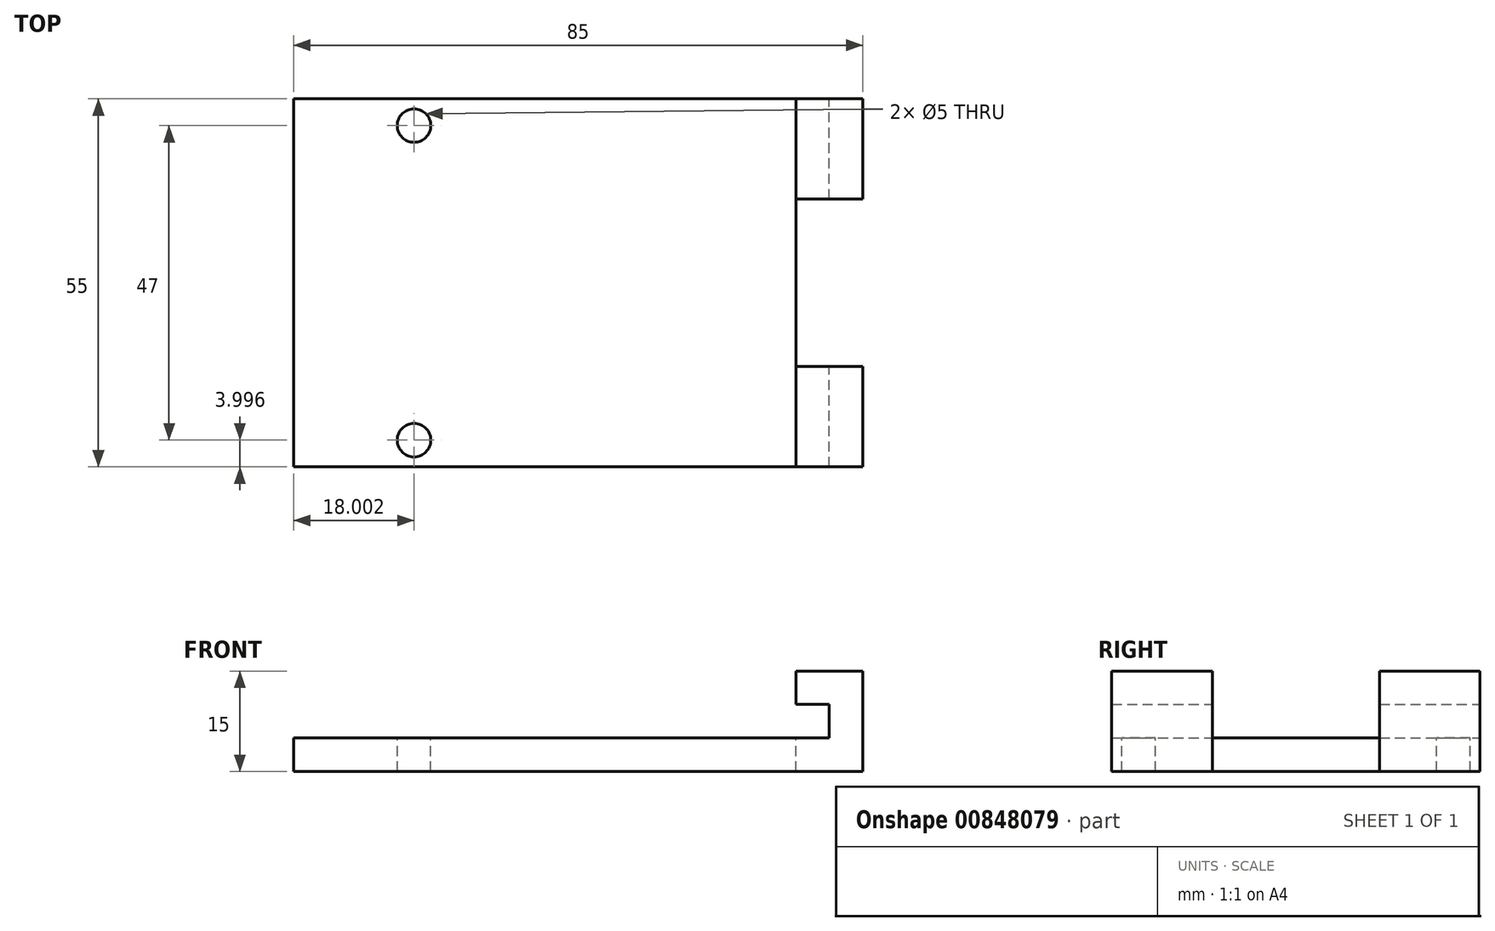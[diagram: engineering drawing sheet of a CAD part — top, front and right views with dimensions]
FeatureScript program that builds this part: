
annotation { "Feature Type Name" : "Feature", "Feature Type Description" : "" }
export const myFeature = defineFeature(function(context is Context, id is Id, definition is map)
    precondition{}
    {
        {
            var Q0;
            Q0=qCreatedBy(makeId("Top.planeOp"),FACE);
            var sketch = newSketch(context, id + "F0", { "sketchPlane" : qUnion([Q0])});
            skLineSegment(sketch, "E0.bottom", {"start": v(-43.19, 22.84) * mm, "end": v(41.81, 22.84) * mm});
            skLineSegment(sketch, "E0.top", {"start": v(-43.19, -32.16) * mm, "end": v(41.81, -32.16) * mm});
            skLineSegment(sketch, "E0.left", {"start": v(-43.19, 22.84) * mm, "end": v(-43.19, -32.16) * mm});
            skLineSegment(sketch, "E0.right", {"start": v(41.81, 22.84) * mm, "end": v(41.81, -32.16) * mm});
            skSolve(sketch);
        }
        {
            var Q0;
            Q0=makeQuery(id+"F0.imprint","IMPRINT",FACE,{"disambiguationData":[TD([[makeQuery(id+"F0.imprint","IMPRINT",EDGE,{"derivedFrom":sQuery(id+"F0.wireOp",EDGE,"E0.bottom")}),-1.0]])]});
            extrude(context, id + "F1", {"entities" : qUnion([Q0]), "depth" : 5 * mm, "offsetDistance" : 25 * mm});
        }
        {
            var Q0;
            Q0=makeQuery(id+"F1.opExtrude","SWEPT_FACE",FACE,{"disambiguationData":[OSD([sQuery(id+"F0.wireOp",EDGE,"E0.right")])]});
            var sketch = newSketch(context, id + "F2", { "sketchPlane" : qUnion([Q0])});
            skLineSegment(sketch, "E1.bottom", {"start": v(-32.16, 0) * mm, "end": v(22.84, 0) * mm});
            skLineSegment(sketch, "E1.top", {"start": v(-32.16, 10) * mm, "end": v(22.84, 10) * mm});
            skLineSegment(sketch, "E1.left", {"start": v(-32.16, 0) * mm, "end": v(-32.16, 10) * mm});
            skLineSegment(sketch, "E1.right", {"start": v(22.84, 0) * mm, "end": v(22.84, 10) * mm});
            skSolve(sketch);
        }
        {
            var Q0;
            Q0 = qSketchRegion(id + "F2", true);
            extrude(context, id + "F3", {"entities" : qUnion([Q0]), "operationType" : NewBodyOperationType.ADD, "oppositeDirection" : true, "depth" : 5 * mm, "offsetDistance" : 25 * mm});
        }
        {
            var Q0;
            Q0=makeQuery(id+"F3.boolean.opBoolean","MERGE",FACE,{"derivedFrom":[makeQuery(id+"F1.opExtrude","SWEPT_FACE",FACE,{"disambiguationData":[OSD([sQuery(id+"F0.wireOp",EDGE,"E0.right")])]}),makeQuery(id+"F3.opExtrude","CAP_FACE",FACE,{"disambiguationData":[OSD([sQuery(id+"F2.wireOp",EDGE,"E1.bottom"),sQuery(id+"F2.wireOp",EDGE,"E1.top"),sQuery(id+"F2.wireOp",EDGE,"E1.left"),sQuery(id+"F2.wireOp",EDGE,"E1.right")])],"isStart":true})]});
            var sketch = newSketch(context, id + "F4", { "sketchPlane" : qUnion([Q0])});
            skLineSegment(sketch, "E2.top", {"start": v(-32.16, 15) * mm, "end": v(22.84, 15) * mm});
            skLineSegment(sketch, "E3", {"start": v(-32.16, 15) * mm, "end": v(-32.16, 10) * mm});
            skLineSegment(sketch, "E4", {"start": v(22.84, 15) * mm, "end": v(22.84, 10) * mm});
            skLineSegment(sketch, "E5", {"start": v(22.84, 10) * mm, "end": v(-32.16, 10) * mm});
            skSolve(sketch);
        }
        {
            var Q0;
            Q0=makeQuery(id+"F4.imprint","IMPRINT",FACE,{"disambiguationData":[TD([[makeQuery(id+"F4.imprint","IMPRINT",EDGE,{"derivedFrom":sQuery(id+"F4.wireOp",EDGE,"E2.top")}),-1.0]])]});
            extrude(context, id + "F5", {"entities" : qUnion([Q0]), "operationType" : NewBodyOperationType.ADD, "oppositeDirection" : true, "depth" : 10 * mm, "offsetDistance" : 25 * mm});
        }
        {
            var Q0;
            Q0=makeQuery(id+"F5.opExtrude","SWEPT_FACE",FACE,{"disambiguationData":[OSD([sQuery(id+"F4.wireOp",EDGE,"E2.top")])]});
            var sketch = newSketch(context, id + "F6", { "sketchPlane" : qUnion([Q0])});
            skLineSegment(sketch, "E6.bottom", {"start": v(22.42, 7.84) * mm, "end": v(47, 7.84) * mm});
            skLineSegment(sketch, "E6.top", {"start": v(22.42, -17.16) * mm, "end": v(47, -17.16) * mm});
            skLineSegment(sketch, "E6.left", {"start": v(22.42, 7.84) * mm, "end": v(22.42, -17.16) * mm});
            skLineSegment(sketch, "E6.right", {"start": v(47, 7.84) * mm, "end": v(47, -17.16) * mm});
            skSolve(sketch);
        }
        {
            var Q0;
            {var subQ0=sQuery(id+"F6.wireOp",EDGE,"E6.bottom");var subQ1=sQuery(id+"F4.wireOp",EDGE,"E2.top");var subQ2=makeQuery(id+"F5.opExtrude","CAP_EDGE",EDGE,{"disambiguationData":[OSD([subQ1])],"isStart":false});var subQ3=makeQuery(id+"F6.imprint","INTERSECT",VERTEX,{"derivedFrom":[subQ2,subQ0]});Q0=makeQuery(id+"F6.imprint","IMPRINT",FACE,{"disambiguationData":[TD([[makeQuery(id+"F6.imprint","IMPRINT",EDGE,{"disambiguationData":[TD([[subQ3,-1.0]])],"derivedFrom":subQ0}),-1.0]])]});}
            extrude(context, id + "F7", {"entities" : qUnion([Q0]), "operationType" : NewBodyOperationType.REMOVE, "oppositeDirection" : true, "depth" : 23.6 * mm, "offsetDistance" : 25 * mm});
        }
        {
            var Q0;
            Q0=makeQuery(id+"F1.opExtrude","CAP_FACE",FACE,{"disambiguationData":[OSD([sQuery(id+"F0.wireOp",EDGE,"E0.bottom"),sQuery(id+"F0.wireOp",EDGE,"E0.top"),sQuery(id+"F0.wireOp",EDGE,"E0.left"),sQuery(id+"F0.wireOp",EDGE,"E0.right")])],"isStart":false});
            var sketch = newSketch(context, id + "F8", { "sketchPlane" : qUnion([Q0])});
            skCircle(sketch, "E7", {"center": v(-25.19, -28.16) * mm, "radius": 2.5 * mm});
            skCircle(sketch, "E8", {"center": v(-25.19, 18.84) * mm, "radius": 2.5 * mm});
            skSolve(sketch);
        }
        {
            var Q0;
            Q0 = qSketchRegion(id + "F8", true);
            extrude(context, id + "F9", {"entities" : qUnion([Q0]), "operationType" : NewBodyOperationType.REMOVE, "oppositeDirection" : true, "depth" : 25 * mm, "offsetDistance" : 25 * mm});
        }
    });
